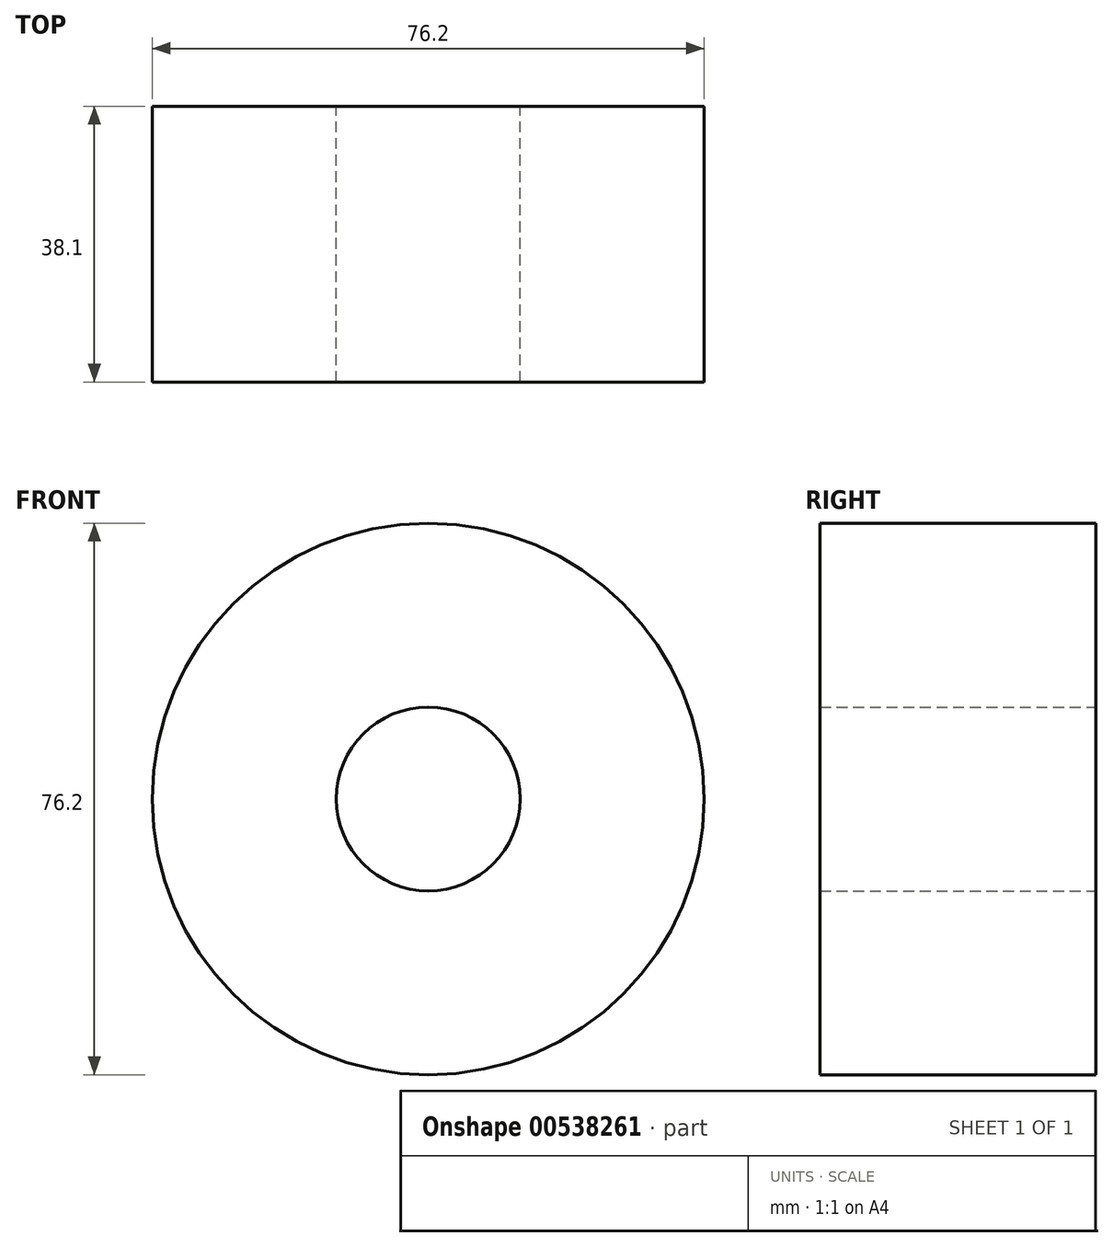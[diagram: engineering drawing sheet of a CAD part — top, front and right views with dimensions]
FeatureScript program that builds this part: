
annotation { "Feature Type Name" : "Feature", "Feature Type Description" : "" }
export const myFeature = defineFeature(function(context is Context, id is Id, definition is map)
    precondition{}
    {
        {
            var Q0;
            Q0=qCreatedBy(makeId("Front.planeOp"),FACE);
            var sketch = newSketch(context, id + "F0", { "sketchPlane" : qUnion([Q0])});
            skCircle(sketch, "E0", {"center": v(0, 0) * mm, "radius": 38.1 * mm});
            skCircle(sketch, "E1", {"center": v(0, 0) * mm, "radius": 12.7 * mm});
            skSolve(sketch);
        }
        {
            var Q0;
            Q0=makeQuery(id+"F0.imprint","IMPRINT",FACE,{"disambiguationData":[TD([[makeQuery(id+"F0.imprint","IMPRINT",EDGE,{"derivedFrom":sQuery(id+"F0.wireOp",EDGE,"E0")}),1.0]])]});
            extrude(context, id + "F1", {"entities" : qUnion([Q0]), "endBound" : BoundingType.SYMMETRIC, "depth" : 38.1 * mm, "offsetDistance" : 25.4 * mm});
        }
    });
